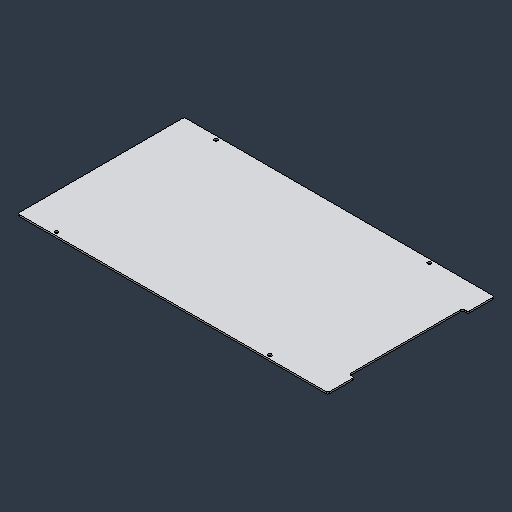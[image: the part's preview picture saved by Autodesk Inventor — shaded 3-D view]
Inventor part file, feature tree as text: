
AUTODESK INVENTOR PART (.ipt)
format: ipt  version: 2024.3 (Build 283343000, 343)  size: 88,576 bytes
history: native  units: mm (DEFAULTED — no unit token found)
features: fillet x1
ambient origin geometry x8: Origin, YZ Plane, XZ Plane, XY Plane, X Axis, Y Axis, Z Axis, Center Point
bodies: Solid1 (feature_tree)
feature tree (1):
  fillet  "Fillet2"  [1 undecoded]
note: 1 required parameter value undecoded (feature->parameter linkage not recoverable at this tier; creation-order binding heuristic only, values carry confidence <= 0.55)
